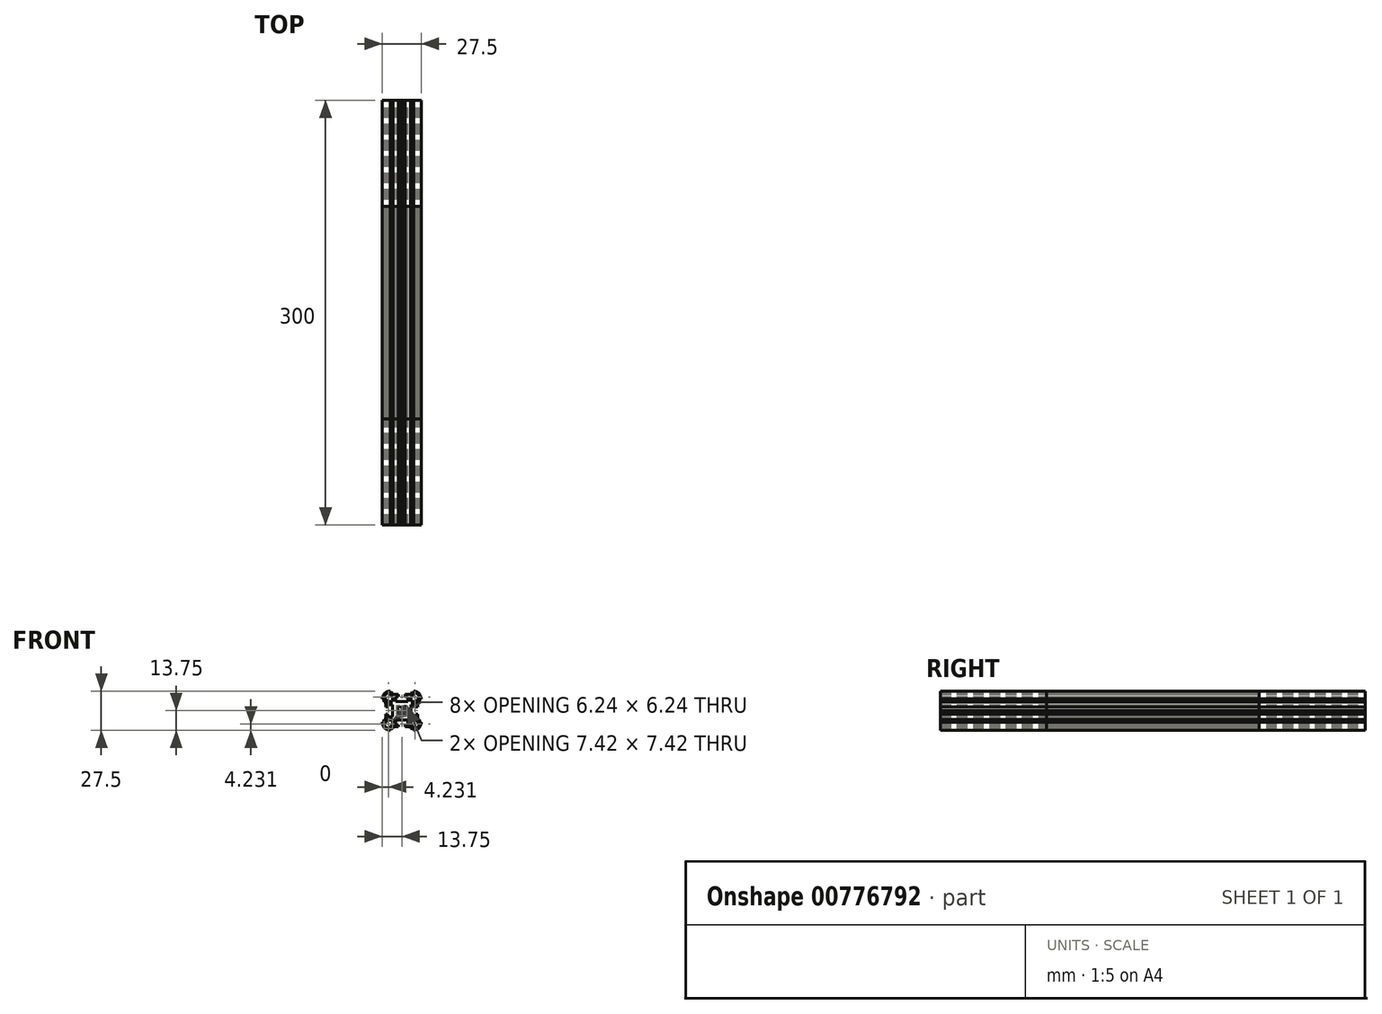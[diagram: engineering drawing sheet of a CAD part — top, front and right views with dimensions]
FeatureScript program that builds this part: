
annotation { "Feature Type Name" : "Feature", "Feature Type Description" : "" }
export const myFeature = defineFeature(function(context is Context, id is Id, definition is map)
    precondition{}
    {
        {
            var Q0;
            Q0=qCreatedBy(makeId("Front.planeOp"),FACE);
            var sketch = newSketch(context, id + "F0", { "sketchPlane" : qUnion([Q0])});
            skLineSegment(sketch, "E0.1", {"start": v(6.25, 12.65) * mm, "end": v(8.25, 12.65) * mm});
            skLineSegment(sketch, "E0.2", {"start": v(2.5, 9.9) * mm, "end": v(2.5, 11.4) * mm});
            skLineSegment(sketch, "E0.3", {"start": v(2.5, 11.4) * mm, "end": v(6.25, 11.4) * mm});
            skLineSegment(sketch, "E0.4", {"start": v(4.25, 6.4) * mm, "end": v(4.25, 9.9) * mm});
            skLineSegment(sketch, "E0.5", {"start": v(6.25, 11.4) * mm, "end": v(6.25, 12.65) * mm});
            skLineSegment(sketch, "E0.6", {"start": v(8.25, 12.65) * mm, "end": v(8.25, 13.75) * mm});
            skLineSegment(sketch, "E0.8", {"start": v(4.25, 9.9) * mm, "end": v(2.5, 9.9) * mm});
            skLineSegment(sketch, "E1", {"start": v(0.2, 6.4) * mm, "end": v(4.25, 6.4) * mm});
            skLineSegment(sketch, "E2", {"start": v(0, 0) * mm, "end": v(16.45, 16.45) * mm, "construction": true});
            skArc(sketch, "E3", {"start": v(12.14, 12.14) * mm, "mid": v(10.35, 13.33) * mm, "end": v(8.25, 13.75) * mm});
            skLineSegment(sketch, "E4", {"start": v(0, 6.2) * mm, "end": v(0.2, 6.4) * mm});
            skArc(sketch, "E5", {"start": v(0.84, 2.25) * mm, "mid": v(0.42, 2.36) * mm, "end": v(0, 2.4) * mm});
            skLineSegment(sketch, "E6", {"start": v(0.84, 2.25) * mm, "end": v(2.3, 3.71) * mm});
            skLineSegment(sketch, "E7", {"start": v(2.3, 3.71) * mm, "end": v(3, 3) * mm});
            skArc(sketch, "E8.0", {"start": v(11.43, 11.43) * mm, "mid": v(10.43, 12.19) * mm, "end": v(9.25, 12.64) * mm});
            skLineSegment(sketch, "E8.1", {"start": v(9.25, 11.65) * mm, "end": v(9.25, 12.64) * mm});
            skLineSegment(sketch, "E8.2", {"start": v(7.25, 11.65) * mm, "end": v(9.25, 11.65) * mm});
            skLineSegment(sketch, "E8.3", {"start": v(7.25, 9.9) * mm, "end": v(7.25, 11.65) * mm});
            skLineSegment(sketch, "E9", {"start": v(7.25, 9.9) * mm, "end": v(6.4, 9.9) * mm});
            skLineSegment(sketch, "E10", {"start": v(6.4, 9.9) * mm, "end": v(6.4, 6.4) * mm});
            skSolve(sketch);
        }
        {
            var Q0;
            Q0=qCreatedBy(makeId("Front.planeOp"),FACE);
            var sketch = newSketch(context, id + "F1", { "sketchPlane" : qUnion([Q0])});
            skArc(sketch, "E11.0", {"start": v(0.84, 2.25) * mm, "mid": v(0.42, 2.36) * mm, "end": v(0, 2.4) * mm});
            skLineSegment(sketch, "E11.1", {"start": v(0.84, 2.25) * mm, "end": v(2.3, 3.71) * mm});
            skLineSegment(sketch, "E11.2", {"start": v(2.3, 3.71) * mm, "end": v(3, 3) * mm});
            skLineSegment(sketch, "E12.0", {"start": v(0, 6.2) * mm, "end": v(0.2, 6.4) * mm});
            skLineSegment(sketch, "E12.1", {"start": v(0.2, 6.4) * mm, "end": v(4.25, 6.4) * mm});
            skLineSegment(sketch, "E12.2", {"start": v(4.25, 6.4) * mm, "end": v(4.25, 9.9) * mm});
            skLineSegment(sketch, "E13.0", {"start": v(6.4, 9.9) * mm, "end": v(6.4, 6.4) * mm});
            skLineSegment(sketch, "E13.1", {"start": v(7.25, 9.9) * mm, "end": v(6.4, 9.9) * mm});
            skLineSegment(sketch, "E13.2", {"start": v(7.25, 9.9) * mm, "end": v(7.25, 11.65) * mm});
            skLineSegment(sketch, "E14.0", {"start": v(4.25, 9.9) * mm, "end": v(2.5, 9.9) * mm});
            skLineSegment(sketch, "E14.1", {"start": v(2.5, 9.9) * mm, "end": v(2.5, 11.4) * mm});
            skLineSegment(sketch, "E14.2", {"start": v(2.5, 11.4) * mm, "end": v(6.25, 11.4) * mm});
            skLineSegment(sketch, "E14.3", {"start": v(6.25, 12.65) * mm, "end": v(8.25, 12.65) * mm});
            skArc(sketch, "E14.4", {"start": v(12.14, 12.14) * mm, "mid": v(10.35, 13.33) * mm, "end": v(8.25, 13.75) * mm});
            skArc(sketch, "E14.5", {"start": v(11.43, 11.43) * mm, "mid": v(10.43, 12.19) * mm, "end": v(9.25, 12.64) * mm});
            skLineSegment(sketch, "E14.6", {"start": v(7.25, 11.65) * mm, "end": v(9.25, 11.65) * mm});
            skLineSegment(sketch, "E14.7", {"start": v(8.25, 12.65) * mm, "end": v(8.25, 13.75) * mm});
            skLineSegment(sketch, "E14.8", {"start": v(9.25, 11.65) * mm, "end": v(9.25, 12.64) * mm});
            skLineSegment(sketch, "E14.9", {"start": v(6.25, 11.4) * mm, "end": v(6.25, 12.65) * mm});
            skLineSegment(sketch, "E15.MirrorCS", {"start": v(6.2, 0) * mm, "end": v(6.4, 0.2) * mm});
            skArc(sketch, "E16.MirrorCS", {"start": v(2.25, 0.84) * mm, "mid": v(2.36, 0.42) * mm, "end": v(2.4, 0) * mm});
            skLineSegment(sketch, "E17.MirrorCS", {"start": v(9.9, 2.5) * mm, "end": v(11.4, 2.5) * mm});
            skLineSegment(sketch, "E18.MirrorCS", {"start": v(12.65, 8.25) * mm, "end": v(13.75, 8.25) * mm});
            skLineSegment(sketch, "E19.MirrorCS", {"start": v(3.71, 2.3) * mm, "end": v(3, 3) * mm});
            skLineSegment(sketch, "E20.MirrorCS", {"start": v(11.65, 9.25) * mm, "end": v(12.64, 9.25) * mm});
            skLineSegment(sketch, "E21.MirrorCS", {"start": v(11.4, 6.25) * mm, "end": v(12.65, 6.25) * mm});
            skLineSegment(sketch, "E22.MirrorCS", {"start": v(9.9, 7.25) * mm, "end": v(11.65, 7.25) * mm});
            skArc(sketch, "E23.MirrorCS", {"start": v(11.43, 11.43) * mm, "mid": v(12.19, 10.43) * mm, "end": v(12.64, 9.25) * mm});
            skLineSegment(sketch, "E24.MirrorCS", {"start": v(9.9, 4.25) * mm, "end": v(9.9, 2.5) * mm});
            skLineSegment(sketch, "E25.MirrorCS", {"start": v(12.65, 6.25) * mm, "end": v(12.65, 8.25) * mm});
            skLineSegment(sketch, "E26.MirrorCS", {"start": v(6.4, 0.2) * mm, "end": v(6.4, 4.25) * mm});
            skLineSegment(sketch, "E27.MirrorCS", {"start": v(11.4, 2.5) * mm, "end": v(11.4, 6.25) * mm});
            skLineSegment(sketch, "E28.MirrorCS", {"start": v(2.25, 0.84) * mm, "end": v(3.71, 2.3) * mm});
            skArc(sketch, "E29.MirrorCS", {"start": v(12.14, 12.14) * mm, "mid": v(13.33, 10.35) * mm, "end": v(13.75, 8.25) * mm});
            skLineSegment(sketch, "E30.MirrorCS", {"start": v(6.4, 4.25) * mm, "end": v(9.9, 4.25) * mm});
            skLineSegment(sketch, "E31.MirrorCS", {"start": v(11.65, 7.25) * mm, "end": v(11.65, 9.25) * mm});
            skLineSegment(sketch, "E32.MirrorCS", {"start": v(9.9, 7.25) * mm, "end": v(9.9, 6.4) * mm});
            skLineSegment(sketch, "E33.MirrorCS", {"start": v(9.9, 6.4) * mm, "end": v(6.4, 6.4) * mm});
            skLineSegment(sketch, "E34.MirrorCS", {"start": v(0, -6.2) * mm, "end": v(0.2, -6.4) * mm});
            skLineSegment(sketch, "E35.MirrorCS", {"start": v(9.25, -11.65) * mm, "end": v(9.25, -12.64) * mm});
            skLineSegment(sketch, "E36.MirrorCS", {"start": v(2.5, -9.9) * mm, "end": v(2.5, -11.4) * mm});
            skArc(sketch, "E37.MirrorCS", {"start": v(0.84, -2.25) * mm, "mid": v(0.42, -2.36) * mm, "end": v(0, -2.4) * mm});
            skLineSegment(sketch, "E38.MirrorCS", {"start": v(6.2, 0) * mm, "end": v(6.4, -0.2) * mm});
            skLineSegment(sketch, "E39.MirrorCS", {"start": v(12.65, -8.25) * mm, "end": v(13.75, -8.25) * mm});
            skLineSegment(sketch, "E40.MirrorCS", {"start": v(8.25, -12.65) * mm, "end": v(8.25, -13.75) * mm});
            skLineSegment(sketch, "E41.MirrorCS", {"start": v(11.65, -9.25) * mm, "end": v(12.64, -9.25) * mm});
            skLineSegment(sketch, "E42.MirrorCS", {"start": v(2.3, -3.71) * mm, "end": v(3, -3) * mm});
            skLineSegment(sketch, "E43.MirrorCS", {"start": v(9.9, -2.5) * mm, "end": v(11.4, -2.5) * mm});
            skLineSegment(sketch, "E44.MirrorCS", {"start": v(6.25, -11.4) * mm, "end": v(6.25, -12.65) * mm});
            skLineSegment(sketch, "E45.MirrorCS", {"start": v(3.71, -2.3) * mm, "end": v(3, -3) * mm});
            skLineSegment(sketch, "E46.MirrorCS", {"start": v(11.4, -6.25) * mm, "end": v(12.65, -6.25) * mm});
            skArc(sketch, "E47.MirrorCS", {"start": v(2.25, -0.84) * mm, "mid": v(2.36, -0.42) * mm, "end": v(2.4, 0) * mm});
            skLineSegment(sketch, "E48.MirrorCS", {"start": v(6.4, -4.25) * mm, "end": v(9.9, -4.25) * mm});
            skLineSegment(sketch, "E49.MirrorCS", {"start": v(9.9, -6.4) * mm, "end": v(6.4, -6.4) * mm});
            skLineSegment(sketch, "E50.MirrorCS", {"start": v(6.25, -12.65) * mm, "end": v(8.25, -12.65) * mm});
            skLineSegment(sketch, "E51.MirrorCS", {"start": v(2.25, -0.84) * mm, "end": v(3.71, -2.3) * mm});
            skLineSegment(sketch, "E52.MirrorCS", {"start": v(6.4, -0.2) * mm, "end": v(6.4, -4.25) * mm});
            skLineSegment(sketch, "E53.MirrorCS", {"start": v(0.2, -6.4) * mm, "end": v(4.25, -6.4) * mm});
            skLineSegment(sketch, "E54.MirrorCS", {"start": v(4.25, -9.9) * mm, "end": v(2.5, -9.9) * mm});
            skLineSegment(sketch, "E55.MirrorCS", {"start": v(4.25, -6.4) * mm, "end": v(4.25, -9.9) * mm});
            skArc(sketch, "E56.MirrorCS", {"start": v(11.43, -11.43) * mm, "mid": v(12.19, -10.43) * mm, "end": v(12.64, -9.25) * mm});
            skArc(sketch, "E57.MirrorCS", {"start": v(11.43, -11.43) * mm, "mid": v(10.43, -12.19) * mm, "end": v(9.25, -12.64) * mm});
            skLineSegment(sketch, "E58.MirrorCS", {"start": v(9.9, -7.25) * mm, "end": v(9.9, -6.4) * mm});
            skLineSegment(sketch, "E59.MirrorCS", {"start": v(11.4, -2.5) * mm, "end": v(11.4, -6.25) * mm});
            skLineSegment(sketch, "E60.MirrorCS", {"start": v(6.4, -9.9) * mm, "end": v(6.4, -6.4) * mm});
            skLineSegment(sketch, "E61.MirrorCS", {"start": v(7.25, -9.9) * mm, "end": v(6.4, -9.9) * mm});
            skLineSegment(sketch, "E62.MirrorCS", {"start": v(0.84, -2.25) * mm, "end": v(2.3, -3.71) * mm});
            skLineSegment(sketch, "E63.MirrorCS", {"start": v(12.65, -6.25) * mm, "end": v(12.65, -8.25) * mm});
            skLineSegment(sketch, "E64.MirrorCS", {"start": v(9.9, -4.25) * mm, "end": v(9.9, -2.5) * mm});
            skLineSegment(sketch, "E65.MirrorCS", {"start": v(7.25, -11.65) * mm, "end": v(9.25, -11.65) * mm});
            skArc(sketch, "E66.MirrorCS", {"start": v(12.14, -12.14) * mm, "mid": v(10.35, -13.33) * mm, "end": v(8.25, -13.75) * mm});
            skLineSegment(sketch, "E67.MirrorCS", {"start": v(9.9, -7.25) * mm, "end": v(11.65, -7.25) * mm});
            skLineSegment(sketch, "E68.MirrorCS", {"start": v(11.65, -7.25) * mm, "end": v(11.65, -9.25) * mm});
            skLineSegment(sketch, "E69.MirrorCS", {"start": v(7.25, -9.9) * mm, "end": v(7.25, -11.65) * mm});
            skLineSegment(sketch, "E70.MirrorCS", {"start": v(2.5, -11.4) * mm, "end": v(6.25, -11.4) * mm});
            skArc(sketch, "E71.MirrorCS", {"start": v(12.14, -12.14) * mm, "mid": v(13.33, -10.35) * mm, "end": v(13.75, -8.25) * mm});
            skLineSegment(sketch, "E72.MirrorCS", {"start": v(-6.2, 0) * mm, "end": v(-6.4, -0.2) * mm});
            skLineSegment(sketch, "E73.MirrorCS", {"start": v(-6.2, 0) * mm, "end": v(-6.4, 0.2) * mm});
            skLineSegment(sketch, "E74.MirrorCS", {"start": v(0, 6.2) * mm, "end": v(-0.2, 6.4) * mm});
            skLineSegment(sketch, "E75.MirrorCS", {"start": v(-9.25, 11.65) * mm, "end": v(-9.25, 12.64) * mm});
            skLineSegment(sketch, "E76.MirrorCS", {"start": v(-8.25, -12.65) * mm, "end": v(-8.25, -13.75) * mm});
            skLineSegment(sketch, "E77.MirrorCS", {"start": v(-12.65, -8.25) * mm, "end": v(-13.75, -8.25) * mm});
            skLineSegment(sketch, "E78.MirrorCS", {"start": v(-2.3, -3.71) * mm, "end": v(-3, -3) * mm});
            skLineSegment(sketch, "E79.MirrorCS", {"start": v(-2.3, 3.71) * mm, "end": v(-3, 3) * mm});
            skLineSegment(sketch, "E80.MirrorCS", {"start": v(-11.65, 9.25) * mm, "end": v(-12.64, 9.25) * mm});
            skLineSegment(sketch, "E81.MirrorCS", {"start": v(-11.4, 6.25) * mm, "end": v(-12.65, 6.25) * mm});
            skLineSegment(sketch, "E82.MirrorCS", {"start": v(-9.25, -11.65) * mm, "end": v(-9.25, -12.64) * mm});
            skLineSegment(sketch, "E83.MirrorCS", {"start": v(-3.71, 2.3) * mm, "end": v(-3, 3) * mm});
            skLineSegment(sketch, "E84.MirrorCS", {"start": v(-3.71, -2.3) * mm, "end": v(-3, -3) * mm});
            skLineSegment(sketch, "E85.MirrorCS", {"start": v(0, -6.2) * mm, "end": v(-0.2, -6.4) * mm});
            skLineSegment(sketch, "E86.MirrorCS", {"start": v(-9.9, 2.5) * mm, "end": v(-11.4, 2.5) * mm});
            skArc(sketch, "E87.MirrorCS", {"start": v(-2.25, -0.84) * mm, "mid": v(-2.36, -0.42) * mm, "end": v(-2.4, 0) * mm});
            skLineSegment(sketch, "E88.MirrorCS", {"start": v(-11.4, -6.25) * mm, "end": v(-12.65, -6.25) * mm});
            skArc(sketch, "E89.MirrorCS", {"start": v(-2.25, 0.84) * mm, "mid": v(-2.36, 0.42) * mm, "end": v(-2.4, 0) * mm});
            skLineSegment(sketch, "E90.MirrorCS", {"start": v(-6.25, 11.4) * mm, "end": v(-6.25, 12.65) * mm});
            skLineSegment(sketch, "E91.MirrorCS", {"start": v(-8.25, 12.65) * mm, "end": v(-8.25, 13.75) * mm});
            skLineSegment(sketch, "E92.MirrorCS", {"start": v(-12.65, 8.25) * mm, "end": v(-13.75, 8.25) * mm});
            skLineSegment(sketch, "E93.MirrorCS", {"start": v(-6.25, -11.4) * mm, "end": v(-6.25, -12.65) * mm});
            skLineSegment(sketch, "E94.MirrorCS", {"start": v(-11.65, -9.25) * mm, "end": v(-12.64, -9.25) * mm});
            skLineSegment(sketch, "E95.MirrorCS", {"start": v(-9.9, -2.5) * mm, "end": v(-11.4, -2.5) * mm});
            skArc(sketch, "E96.MirrorCS", {"start": v(-0.84, 2.25) * mm, "mid": v(-0.42, 2.36) * mm, "end": v(0, 2.4) * mm});
            skArc(sketch, "E97.MirrorCS", {"start": v(-0.84, -2.25) * mm, "mid": v(-0.42, -2.36) * mm, "end": v(0, -2.4) * mm});
            skLineSegment(sketch, "E98.MirrorCS", {"start": v(-2.5, 11.4) * mm, "end": v(-6.25, 11.4) * mm});
            skLineSegment(sketch, "E99.MirrorCS", {"start": v(-12.65, -6.25) * mm, "end": v(-12.65, -8.25) * mm});
            skLineSegment(sketch, "E100.MirrorCS", {"start": v(-4.25, 9.9) * mm, "end": v(-2.5, 9.9) * mm});
            skLineSegment(sketch, "E101.MirrorCS", {"start": v(-6.4, 4.25) * mm, "end": v(-9.9, 4.25) * mm});
            skLineSegment(sketch, "E102.MirrorCS", {"start": v(-6.4, -0.2) * mm, "end": v(-6.4, -4.25) * mm});
            skLineSegment(sketch, "E103.MirrorCS", {"start": v(-6.25, 12.65) * mm, "end": v(-8.25, 12.65) * mm});
            skLineSegment(sketch, "E104.MirrorCS", {"start": v(-0.2, -6.4) * mm, "end": v(-4.25, -6.4) * mm});
            skArc(sketch, "E105.MirrorCS", {"start": v(-11.43, -11.43) * mm, "mid": v(-12.19, -10.43) * mm, "end": v(-12.64, -9.25) * mm});
            skLineSegment(sketch, "E106.MirrorCS", {"start": v(-7.25, -9.9) * mm, "end": v(-7.25, -11.65) * mm});
            skLineSegment(sketch, "E107.MirrorCS", {"start": v(-9.9, 7.25) * mm, "end": v(-9.9, 6.4) * mm});
            skLineSegment(sketch, "E108.MirrorCS", {"start": v(-9.9, 4.25) * mm, "end": v(-9.9, 2.5) * mm});
            skArc(sketch, "E109.MirrorCS", {"start": v(-12.14, -12.14) * mm, "mid": v(-10.35, -13.33) * mm, "end": v(-8.25, -13.75) * mm});
            skArc(sketch, "E110.MirrorCS", {"start": v(-11.43, 11.43) * mm, "mid": v(-10.43, 12.19) * mm, "end": v(-9.25, 12.64) * mm});
            skLineSegment(sketch, "E111.MirrorCS", {"start": v(-4.25, -6.4) * mm, "end": v(-4.25, -9.9) * mm});
            skLineSegment(sketch, "E112.MirrorCS", {"start": v(-6.4, -9.9) * mm, "end": v(-6.4, -6.4) * mm});
            skLineSegment(sketch, "E113.MirrorCS", {"start": v(-6.25, -12.65) * mm, "end": v(-8.25, -12.65) * mm});
            skArc(sketch, "E114.MirrorCS", {"start": v(-12.14, 12.14) * mm, "mid": v(-10.35, 13.33) * mm, "end": v(-8.25, 13.75) * mm});
            skArc(sketch, "E115.MirrorCS", {"start": v(-12.14, 12.14) * mm, "mid": v(-13.33, 10.35) * mm, "end": v(-13.75, 8.25) * mm});
            skLineSegment(sketch, "E116.MirrorCS", {"start": v(-11.4, 2.5) * mm, "end": v(-11.4, 6.25) * mm});
            skLineSegment(sketch, "E117.MirrorCS", {"start": v(-6.4, -4.25) * mm, "end": v(-9.9, -4.25) * mm});
            skLineSegment(sketch, "E118.MirrorCS", {"start": v(-4.25, 6.4) * mm, "end": v(-4.25, 9.9) * mm});
            skLineSegment(sketch, "E119.MirrorCS", {"start": v(-11.65, 7.25) * mm, "end": v(-11.65, 9.25) * mm});
            skLineSegment(sketch, "E120.MirrorCS", {"start": v(-0.2, 6.4) * mm, "end": v(-4.25, 6.4) * mm});
            skLineSegment(sketch, "E121.MirrorCS", {"start": v(-2.25, 0.84) * mm, "end": v(-3.71, 2.3) * mm});
            skLineSegment(sketch, "E122.MirrorCS", {"start": v(-2.5, -11.4) * mm, "end": v(-6.25, -11.4) * mm});
            skLineSegment(sketch, "E123.MirrorCS", {"start": v(-4.25, -9.9) * mm, "end": v(-2.5, -9.9) * mm});
            skLineSegment(sketch, "E124.MirrorCS", {"start": v(-11.4, -2.5) * mm, "end": v(-11.4, -6.25) * mm});
            skLineSegment(sketch, "E125.MirrorCS", {"start": v(-9.9, -7.25) * mm, "end": v(-9.9, -6.4) * mm});
            skLineSegment(sketch, "E126.MirrorCS", {"start": v(-7.25, 9.9) * mm, "end": v(-6.4, 9.9) * mm});
            skLineSegment(sketch, "E127.MirrorCS", {"start": v(-2.5, 9.9) * mm, "end": v(-2.5, 11.4) * mm});
            skLineSegment(sketch, "E128.MirrorCS", {"start": v(-11.65, -7.25) * mm, "end": v(-11.65, -9.25) * mm});
            skLineSegment(sketch, "E129.MirrorCS", {"start": v(-9.9, -6.4) * mm, "end": v(-6.4, -6.4) * mm});
            skLineSegment(sketch, "E130.MirrorCS", {"start": v(-7.25, -9.9) * mm, "end": v(-6.4, -9.9) * mm});
            skLineSegment(sketch, "E131.MirrorCS", {"start": v(-9.9, 7.25) * mm, "end": v(-11.65, 7.25) * mm});
            skLineSegment(sketch, "E132.MirrorCS", {"start": v(-7.25, 11.65) * mm, "end": v(-9.25, 11.65) * mm});
            skLineSegment(sketch, "E133.MirrorCS", {"start": v(-0.84, -2.25) * mm, "end": v(-2.3, -3.71) * mm});
            skLineSegment(sketch, "E134.MirrorCS", {"start": v(-7.25, -11.65) * mm, "end": v(-9.25, -11.65) * mm});
            skArc(sketch, "E135.MirrorCS", {"start": v(-11.43, -11.43) * mm, "mid": v(-10.43, -12.19) * mm, "end": v(-9.25, -12.64) * mm});
            skLineSegment(sketch, "E136.MirrorCS", {"start": v(-9.9, -7.25) * mm, "end": v(-11.65, -7.25) * mm});
            skLineSegment(sketch, "E137.MirrorCS", {"start": v(-12.65, 6.25) * mm, "end": v(-12.65, 8.25) * mm});
            skLineSegment(sketch, "E138.MirrorCS", {"start": v(-0.84, 2.25) * mm, "end": v(-2.3, 3.71) * mm});
            skArc(sketch, "E139.MirrorCS", {"start": v(-11.43, 11.43) * mm, "mid": v(-12.19, 10.43) * mm, "end": v(-12.64, 9.25) * mm});
            skArc(sketch, "E140.MirrorCS", {"start": v(-12.14, -12.14) * mm, "mid": v(-13.33, -10.35) * mm, "end": v(-13.75, -8.25) * mm});
            skLineSegment(sketch, "E141.MirrorCS", {"start": v(-6.4, 0.2) * mm, "end": v(-6.4, 4.25) * mm});
            skLineSegment(sketch, "E142.MirrorCS", {"start": v(-2.25, -0.84) * mm, "end": v(-3.71, -2.3) * mm});
            skLineSegment(sketch, "E143.MirrorCS", {"start": v(-7.25, 9.9) * mm, "end": v(-7.25, 11.65) * mm});
            skLineSegment(sketch, "E144.MirrorCS", {"start": v(-2.5, -9.9) * mm, "end": v(-2.5, -11.4) * mm});
            skLineSegment(sketch, "E145.MirrorCS", {"start": v(-9.9, -4.25) * mm, "end": v(-9.9, -2.5) * mm});
            skLineSegment(sketch, "E146.MirrorCS", {"start": v(-9.9, 6.4) * mm, "end": v(-6.4, 6.4) * mm});
            skLineSegment(sketch, "E147.MirrorCS", {"start": v(-6.4, 9.9) * mm, "end": v(-6.4, 6.4) * mm});
            skSolve(sketch);
        }
        {
            var Q0;
            Q0=makeQuery(id+"F1.imprint","IMPRINT",FACE,{"disambiguationData":[TD([[makeQuery(id+"F1.imprint","IMPRINT",EDGE,{"derivedFrom":sQuery(id+"F1.wireOp",EDGE,"E34.MirrorCS")}),1.0]])]});
            extrude(context, id + "F2", {"entities" : qUnion([Q0]), "depth" : 150 * mm, "offsetDistance" : 25 * mm});
        }
        {
            var Q0;
            Q0 = qSketchRegion(id + "F1", true);
            extrude(context, id + "F3", {"entities" : qUnion([Q0]), "depth" : 225 * mm, "offsetDistance" : 25 * mm, "hasSecondDirection" : true, "secondDirectionOppositeDirection" : true, "secondDirectionDepth" : 75 * mm});
        }
    });
